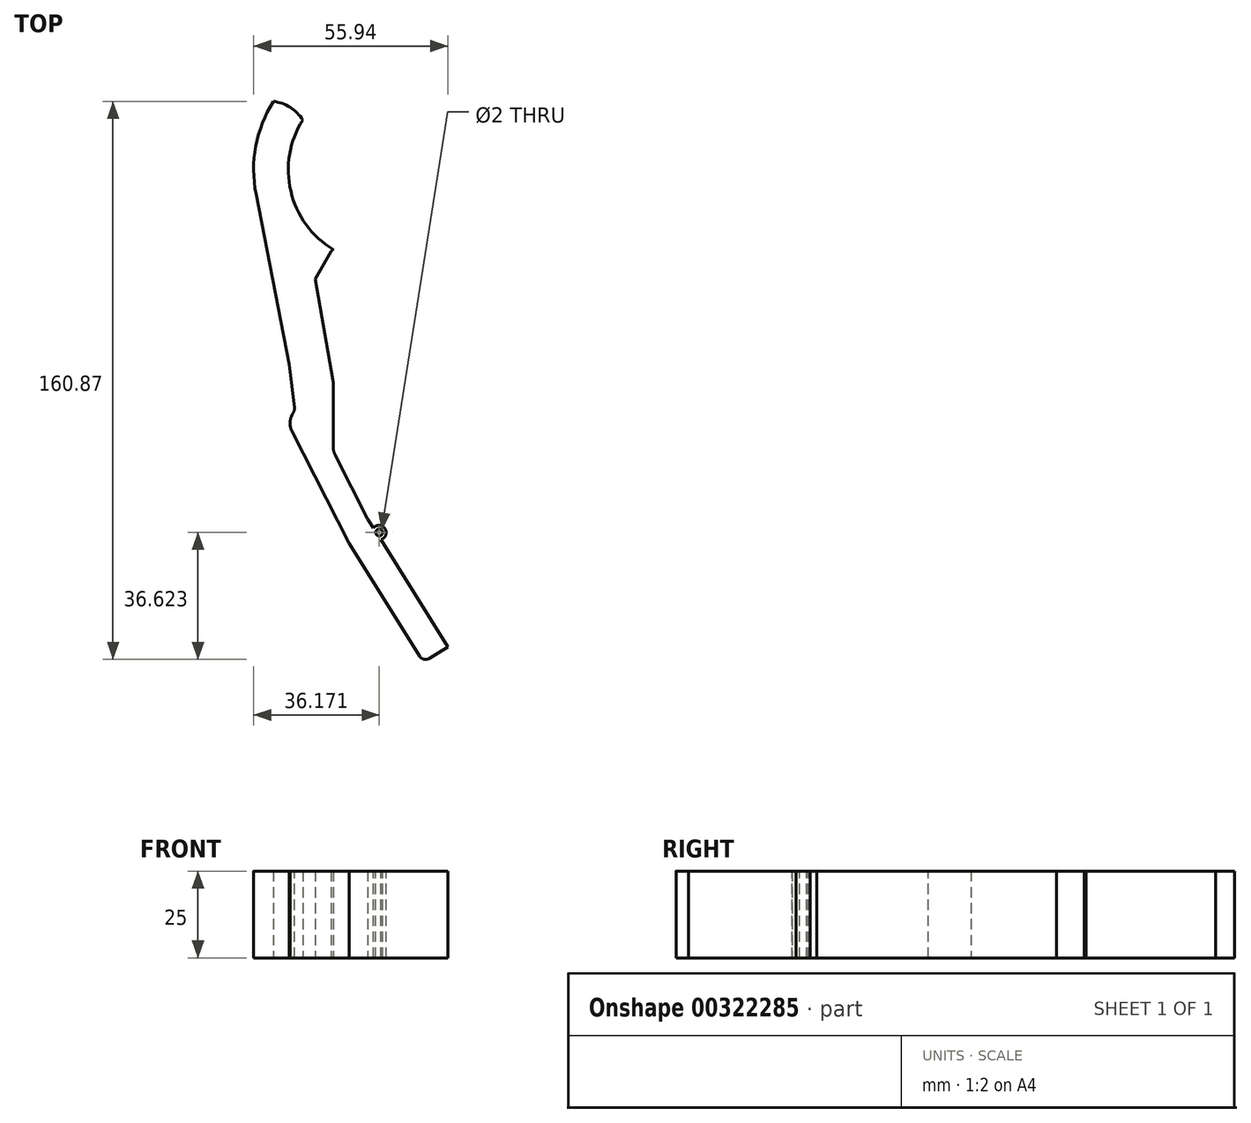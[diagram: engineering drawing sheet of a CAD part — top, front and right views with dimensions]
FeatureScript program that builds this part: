
annotation { "Feature Type Name" : "Feature", "Feature Type Description" : "" }
export const myFeature = defineFeature(function(context is Context, id is Id, definition is map)
    precondition{}
    {
        {
            var Q0;
            Q0=qCreatedBy(makeId("Top.planeOp"),FACE);
            var sketch = newSketch(context, id + "F0", { "sketchPlane" : qUnion([Q0])});
            skLineSegment(sketch, "E0", {"start": v(0, 0) * mm, "end": v(0, 10) * mm});
            skLineSegment(sketch, "E1", {"start": v(0, 10) * mm, "end": v(-23.85, 48.16) * mm});
            skLineSegment(sketch, "E2", {"start": v(-23.85, 48.16) * mm, "end": v(-46.55, 92.71) * mm});
            skLineSegment(sketch, "E3", {"start": v(-46.55, 92.71) * mm, "end": v(-56.09, 141.8) * mm});
            skLineSegment(sketch, "E4", {"start": v(0, 10) * mm, "end": v(0, 20.39) * mm});
            skLineSegment(sketch, "E5", {"start": v(0, 0) * mm, "end": v(-26.5, 42.4) * mm});
            skLineSegment(sketch, "E6", {"start": v(-26.5, 42.4) * mm, "end": v(-44.66, 78.04) * mm});
            skLineSegment(sketch, "E7", {"start": v(-44.66, 78.04) * mm, "end": v(-46.55, 92.71) * mm});
            skPoint(sketch, "E8", {"position": v(-33.83, 67.76) * mm});
            skLineSegment(sketch, "E9", {"start": v(-33.83, 67.76) * mm, "end": v(-33.83, 87.76) * mm});
            skLineSegment(sketch, "E10", {"start": v(-33.83, 87.76) * mm, "end": v(-39.04, 117.3) * mm});
            skLineSegment(sketch, "E11", {"start": v(-39.04, 117.3) * mm, "end": v(-34.04, 125.97) * mm});
            skArc(sketch, "E12", {"start": v(-56.09, 141.8) * mm, "mid": v(-50.15, 127.75) * mm, "end": v(-39.04, 117.3) * mm});
            skArc(sketch, "E13.0", {"start": v(-46.27, 143.7) * mm, "mid": v(-41.94, 133.47) * mm, "end": v(-33.85, 125.85) * mm});
            skArc(sketch, "E14", {"start": v(-33.85, 125.85) * mm, "mid": v(-46.05, 142.7) * mm, "end": v(-42.6, 163.2) * mm});
            skArc(sketch, "E15.0", {"start": v(-39.04, 117.3) * mm, "mid": v(-55.8, 140.41) * mm, "end": v(-51.06, 168.55) * mm});
            skArc(sketch, "E16", {"start": v(-42.6, 163.2) * mm, "mid": v(-46.23, 166.83) * mm, "end": v(-51.06, 168.55) * mm});
            skArc(sketch, "E17", {"start": v(-42.6, 163.2) * mm, "mid": v(-46.1, 142.68) * mm, "end": v(-33.85, 125.85) * mm});
            skArc(sketch, "E18", {"start": v(-33.85, 125.85) * mm, "mid": v(-37.1, 121.98) * mm, "end": v(-39.04, 117.3) * mm});
            skPoint(sketch, "E19", {"position": v(-21.2, 43.92) * mm});
            skSolve(sketch);
        }
        {
            var Q0;
            {var subQ1=sQuery(id+"F0.wireOp",EDGE,"E3");Q0=makeQuery(id+"F0.imprint","IMPRINT",FACE,{"disambiguationData":[TD([[makeQuery(id+"F0.imprint","IMPRINT",EDGE,{"derivedFrom":subQ1}),-1.0]])]});}
            var Q1;
            Q1=makeQuery(id+"F0.imprint","IMPRINT",FACE,{"disambiguationData":[TD([[makeQuery(id+"F0.imprint","IMPRINT",EDGE,{"derivedFrom":sQuery(id+"F0.wireOp",EDGE,"E0")}),1.0]])]});
            extrude(context, id + "F1", {"entities" : qUnion([Q0, Q1]), "depth" : 25 * mm});
        }
        {
            var Q0;
            Q0=qSketchRegion(id+"F0",true);
            extrude(context, id + "F2", {"entities" : qUnion([Q0]), "operationType" : NewBodyOperationType.ADD, "depth" : 25 * mm});
        }
        {
            var Q0;
            Q0=qCreatedBy(makeId("Top.planeOp"),FACE);
            var sketch = newSketch(context, id + "F3", { "sketchPlane" : qUnion([Q0])});
            skCircle(sketch, "E20", {"center": v(0, 0) * mm, "radius": 10.04 * mm});
            skSolve(sketch);
        }
        {
            var Q0;
            Q0=makeQuery(id+"F3.imprint","IMPRINT",FACE,{"disambiguationData":[TD([[makeQuery(id+"F3.imprint","IMPRINT",EDGE,{"derivedFrom":sQuery(id+"F3.wireOp",EDGE,"E20")}),1.0]])]});
            extrude(context, id + "F4", {"entities" : qUnion([Q0]), "operationType" : NewBodyOperationType.ADD, "depth" : 25 * mm});
        }
        {
            var Q0;
            Q0=makeQuery(id+"F1.opExtrude","SWEPT_FACE",FACE,{"disambiguationData":[OSD([sQuery(id+"F0.wireOp",EDGE,"E5")])]});
            var sketch = newSketch(context, id + "F5", { "sketchPlane" : qUnion([Q0])});
            skPoint(sketch, "E21", {"position": v(-10.04, 16.7) * mm});
            skPoint(sketch, "E22", {"position": v(-10.04, 8.4) * mm});
            skLineSegment(sketch, "E23.bottom", {"start": v(-10.04, 25) * mm, "end": v(-15.56, 25) * mm});
            skLineSegment(sketch, "E23.top", {"start": v(-10.04, 16.7) * mm, "end": v(-15.56, 16.7) * mm});
            skLineSegment(sketch, "E23.left", {"start": v(-10.04, 25) * mm, "end": v(-10.04, 16.7) * mm});
            skLineSegment(sketch, "E23.right", {"start": v(-15.56, 25) * mm, "end": v(-15.56, 16.7) * mm});
            skLineSegment(sketch, "E24.bottom", {"start": v(-10.04, 0) * mm, "end": v(-15.06, 0) * mm});
            skLineSegment(sketch, "E24.top", {"start": v(-10.04, 8.4) * mm, "end": v(-15.06, 8.4) * mm});
            skLineSegment(sketch, "E24.left", {"start": v(-10.04, 0) * mm, "end": v(-10.04, 8.4) * mm});
            skLineSegment(sketch, "E24.right", {"start": v(-15.06, 0) * mm, "end": v(-15.06, 8.4) * mm});
            skSolve(sketch);
        }
        {
            var Q0;
            Q0=makeQuery(id+"F5.imprint","IMPRINT",FACE,{"disambiguationData":[TD([[makeQuery(id+"F5.imprint","IMPRINT",EDGE,{"derivedFrom":sQuery(id+"F5.wireOp",EDGE,"E24.bottom")}),-1.0]])]});
            var Q1;
            Q1=makeQuery(id+"F5.imprint","IMPRINT",FACE,{"disambiguationData":[TD([[makeQuery(id+"F5.imprint","IMPRINT",EDGE,{"derivedFrom":sQuery(id+"F5.wireOp",EDGE,"E23.bottom")}),1.0]])]});
            extrude(context, id + "F6", {"entities" : qUnion([Q0, Q1]), "operationType" : NewBodyOperationType.ADD, "depth" : 28.7 * mm});
        }
        {
            var Q0;
            Q0=makeQuery(id+"F6.opExtrude","SWEPT_FACE",FACE,{"disambiguationData":[OSD([sQuery(id+"F5.wireOp",EDGE,"E23.left")])]});
            var Q1;
            Q1=makeQuery(id+"F6.opExtrude","SWEPT_FACE",FACE,{"disambiguationData":[OSD([sQuery(id+"F5.wireOp",EDGE,"E24.left")])]});
            extrude(context, id + "F7", {"entities" : qUnion([Q0, Q1]), "operationType" : NewBodyOperationType.REMOVE, "endBound" : BoundingType.SYMMETRIC, "oppositeDirection" : true, "depth" : 62.6 * mm});
        }
        {
            var Q0;
            {var subQ0=sQuery(id+"F3.wireOp",EDGE,"E20");var subQ1=sQuery(id+"F0.wireOp",EDGE,"E5");Q0=makeQuery(id+"F7.boolean.opBoolean","MERGE",FACE,{"derivedFrom":[makeQuery(id+"F1.opExtrude","SWEPT_FACE",FACE,{"disambiguationData":[OSD([subQ1])]}),makeQuery(id+"F7.opExtrude","SWEPT_FACE",FACE,{"disambiguationData":[OSD([subQ1,subQ0,sQuery(id+"F5.wireOp",EDGE,"E23.left")])]}),makeQuery(id+"F7.opExtrude","SWEPT_FACE",FACE,{"disambiguationData":[OSD([subQ1,subQ0,sQuery(id+"F5.wireOp",EDGE,"E24.left")])]})]});}
            var sketch = newSketch(context, id + "F8", { "sketchPlane" : qUnion([Q0])});
            skLineSegment(sketch, "E25.bottom", {"start": v(-10.04, 8.4) * mm, "end": v(10.04, 8.4) * mm});
            skLineSegment(sketch, "E25.top", {"start": v(-10.04, 0) * mm, "end": v(10.04, 0) * mm});
            skLineSegment(sketch, "E25.left", {"start": v(-10.04, 8.4) * mm, "end": v(-10.04, 0) * mm});
            skLineSegment(sketch, "E25.right", {"start": v(10.04, 8.4) * mm, "end": v(10.04, 0) * mm});
            skLineSegment(sketch, "E26.bottom", {"start": v(-10.04, 16.7) * mm, "end": v(10.04, 16.7) * mm});
            skLineSegment(sketch, "E26.top", {"start": v(-10.04, 25) * mm, "end": v(10.04, 25) * mm});
            skLineSegment(sketch, "E26.left", {"start": v(-10.04, 16.7) * mm, "end": v(-10.04, 25) * mm});
            skLineSegment(sketch, "E26.right", {"start": v(10.04, 16.7) * mm, "end": v(10.04, 25) * mm});
            skSolve(sketch);
        }
        {
            var Q0;
            Q0=makeQuery(id+"F8.imprint","IMPRINT",FACE,{"disambiguationData":[TD([[makeQuery(id+"F8.imprint","IMPRINT",EDGE,{"derivedFrom":sQuery(id+"F8.wireOp",EDGE,"E26.bottom")}),1.0]])]});
            var Q1;
            Q1=makeQuery(id+"F8.imprint","IMPRINT",FACE,{"disambiguationData":[TD([[makeQuery(id+"F8.imprint","IMPRINT",EDGE,{"derivedFrom":sQuery(id+"F8.wireOp",EDGE,"E25.bottom")}),-1.0]])]});
            extrude(context, id + "F9", {"entities" : qUnion([Q0, Q1]), "operationType" : NewBodyOperationType.REMOVE, "oppositeDirection" : true, "depth" : 25 * mm});
        }
        {
            var Q0;
            Q0=sQuery(id+"F0.wireOp",VERTEX,"E0.start");
            var Q1;
            Q1=makeQuery(id+"F1.opExtrude","SWEPT_BODY",BODY,{"disambiguationData":[OSD([sQuery(id+"F0.wireOp",EDGE,"E0"),sQuery(id+"F0.wireOp",EDGE,"E1"),sQuery(id+"F0.wireOp",EDGE,"E2"),sQuery(id+"F0.wireOp",EDGE,"E3"),sQuery(id+"F0.wireOp",EDGE,"E5"),sQuery(id+"F0.wireOp",EDGE,"E6"),sQuery(id+"F0.wireOp",EDGE,"E7"),sQuery(id+"F0.wireOp",EDGE,"E9"),sQuery(id+"F0.wireOp",EDGE,"E10"),sQuery(id+"F0.wireOp",EDGE,"E15.0")])]});
            hole(context, id + "F10", {"style" : HoleStyle.SIMPLE, "endStyle" : HoleEndStyle.THROUGH, "oppositeDirection" : true, "holeDiameter" : 15 * mm, "tappedDepth" : 12 * mm, "tapClearance" : 3, "locations" : qUnion([Q0]), "scope" : qUnion([Q1])});
        }
        {
            var Q0;
            {var subQ0=sQuery(id+"F3.wireOp",EDGE,"E20");var subQ1=sQuery(id+"F0.wireOp",EDGE,"E5");Q0=makeQuery(id+"F7.boolean.opBoolean","MERGE",FACE,{"derivedFrom":[makeQuery(id+"F1.opExtrude","SWEPT_FACE",FACE,{"disambiguationData":[OSD([subQ1])]}),makeQuery(id+"F7.opExtrude","SWEPT_FACE",FACE,{"disambiguationData":[OSD([subQ1,subQ0,sQuery(id+"F5.wireOp",EDGE,"E23.left")])]}),makeQuery(id+"F7.opExtrude","SWEPT_FACE",FACE,{"disambiguationData":[OSD([subQ1,subQ0,sQuery(id+"F5.wireOp",EDGE,"E24.left")])]})]});}
            extrude(context, id + "F11", {"entities" : qUnion([Q0]), "operationType" : NewBodyOperationType.ADD, "depth" : 3 * mm});
        }
        {
            var Q0;
            Q0=makeQuery(id+"F1.opExtrude","SWEPT_FACE",FACE,{"disambiguationData":[OSD([sQuery(id+"F0.wireOp",EDGE,"E6")])]});
            extrude(context, id + "F12", {"entities" : qUnion([Q0]), "operationType" : NewBodyOperationType.ADD, "depth" : 3 * mm});
        }
        {
            var Q0;
            Q0=makeQuery(id+"F11.opExtrude","SWEPT_FACE",FACE,{"disambiguationData":[OSD([sQuery(id+"F0.wireOp",EDGE,"E5"),sQuery(id+"F0.wireOp",EDGE,"E6")])]});
            extrude(context, id + "F13", {"entities" : qUnion([Q0]), "operationType" : NewBodyOperationType.ADD, "depth" : 0.4 * mm});
        }
        {
            var Q0;
            {var subQ0=sQuery(id+"F0.wireOp",EDGE,"E6");var subQ1=sQuery(id+"F0.wireOp",EDGE,"E5");var subQ2=sQuery(id+"F5.wireOp",EDGE,"E23.bottom");var subQ3=sQuery(id+"F3.wireOp",EDGE,"E20");var subQ4=sQuery(id+"F0.wireOp",EDGE,"E15.0");var subQ5=sQuery(id+"F0.wireOp",EDGE,"E10");var subQ6=sQuery(id+"F0.wireOp",EDGE,"E9");var subQ7=sQuery(id+"F0.wireOp",EDGE,"E7");var subQ8=sQuery(id+"F0.wireOp",EDGE,"E3");var subQ9=sQuery(id+"F0.wireOp",EDGE,"E2");var subQ10=sQuery(id+"F0.wireOp",EDGE,"E1");var subQ11=sQuery(id+"F0.wireOp",EDGE,"E0");Q0=makeQuery(id+"F13.boolean.opBoolean","MERGE",FACE,{"derivedFrom":[makeQuery(id+"F12.boolean.opBoolean","MERGE",FACE,{"derivedFrom":[makeQuery(id+"F11.boolean.opBoolean","MERGE",FACE,{"derivedFrom":[makeQuery(id+"F6.boolean.opBoolean","MERGE",FACE,{"derivedFrom":[makeQuery(id+"F4.boolean.opBoolean","MERGE",FACE,{"derivedFrom":[makeQuery(id+"F2.boolean.opBoolean","MERGE",FACE,{"derivedFrom":[makeQuery(id+"F1.opExtrude","CAP_FACE",FACE,{"disambiguationData":[OSD([subQ11,subQ10,subQ9,subQ8,subQ1,subQ0,subQ7,subQ6,subQ5,subQ4])],"isStart":false}),makeQuery(id+"F2.opExtrude","CAP_FACE",FACE,{"disambiguationData":[OSD([subQ11,subQ10,subQ9,subQ8,subQ1,subQ0,subQ7,subQ6,subQ5,sQuery(id+"F0.wireOp",EDGE,"E11"),sQuery(id+"F0.wireOp",EDGE,"E14"),subQ4,sQuery(id+"F0.wireOp",EDGE,"E16"),sQuery(id+"F0.wireOp",EDGE,"E18")])],"isStart":false})]}),makeQuery(id+"F4.opExtrude","CAP_FACE",FACE,{"disambiguationData":[OSD([subQ3])],"isStart":false})]}),makeQuery(id+"F6.opExtrude","SWEPT_FACE",FACE,{"disambiguationData":[OSD([subQ2])]})]}),makeQuery(id+"F11.opExtrude","SWEPT_FACE",FACE,{"disambiguationData":[OSD([subQ1,subQ3,subQ2,sQuery(id+"F5.wireOp",EDGE,"E23.left")])]})]}),makeQuery(id+"F12.opExtrude","SWEPT_FACE",FACE,{"disambiguationData":[OSD([subQ0]),TDD([makeQuery(id+"F1.opExtrude","CAP_EDGE",EDGE,{"disambiguationData":[OSD([subQ0])],"isStart":false})])]})]}),makeQuery(id+"F13.opExtrude","SWEPT_FACE",FACE,{"disambiguationData":[OSD([subQ1,subQ0]),TDD([makeQuery(id+"F11.opExtrude","SWEPT_EDGE",EDGE,{"disambiguationData":[OSD([subQ1,subQ0]),TDD([makeQuery(id+"F1.opExtrude","CAP_VERTEX",VERTEX,{"disambiguationData":[OSD([subQ1,subQ0])],"isStart":false})])]})])]})]});}
            var sketch = newSketch(context, id + "F14", { "sketchPlane" : qUnion([Q0])});
            skArc(sketch, "E27", {"start": v(-47.33, 76.68) * mm, "mid": v(-45.27, 78.9) * mm, "end": v(-45.16, 81.94) * mm});
            skSolve(sketch);
        }
        {
            var Q0;
            Q0=qSketchRegion(id+"F14",true);
            var Q1;
            {var subQ1=sQuery(id+"F0.wireOp",EDGE,"E6");var subQ2=sQuery(id+"F0.wireOp",EDGE,"E7");var subQ3=makeQuery(id+"F12.opExtrude","SWEPT_EDGE",EDGE,{"disambiguationData":[OSD([subQ1,subQ2]),TDD([makeQuery(id+"F1.opExtrude","CAP_VERTEX",VERTEX,{"disambiguationData":[OSD([subQ1,subQ2])],"isStart":false})])]});Q1=makeQuery(id+"F14.imprint","IMPRINT",FACE,{"disambiguationData":[TD([[makeQuery(id+"F14.imprint","IMPRINT",EDGE,{"derivedFrom":subQ3}),1.0]])]});}
            extrude(context, id + "F15", {"entities" : qUnion([Q0, Q1]), "operationType" : NewBodyOperationType.ADD, "oppositeDirection" : true, "depth" : 25 * mm});
        }
        {
            var Q0;
            {var subQ0=sQuery(id+"F0.wireOp",EDGE,"E7");var subQ1=sQuery(id+"F0.wireOp",EDGE,"E6");Q0=makeQuery(id+"F15.boolean.opBoolean","MERGE",EDGE,{"derivedFrom":[makeQuery(id+"F12.opExtrude","CAP_EDGE",EDGE,{"disambiguationData":[OSD([subQ1,subQ0])],"isStart":false}),makeQuery(id+"F15.opExtrude","SWEPT_EDGE",EDGE,{"disambiguationData":[OSD([subQ1,subQ0,sQuery(id+"F14.wireOp",EDGE,"E27")])]})]});}
            fillet(context, id + "F16", {"entities" : qUnion([Q0]), "radius" : 5 * mm, "tangentPropagation" : true, "allowEdgeOverflow" : false});
        }
        {
            var Q0;
            Q0=makeQuery(id+"F1.opExtrude","SWEPT_EDGE",EDGE,{"disambiguationData":[OSD([sQuery(id+"F0.wireOp",EDGE,"E2"),sQuery(id+"F0.wireOp",EDGE,"E9")])]});
            fillet(context, id + "F17", {"entities" : qUnion([Q0]), "radius" : 5 * mm, "tangentPropagation" : true, "allowEdgeOverflow" : false});
        }
        {
            var Q0;
            Q0=makeQuery(id+"F1.opExtrude","SWEPT_EDGE",EDGE,{"disambiguationData":[OSD([sQuery(id+"F0.wireOp",EDGE,"E9"),sQuery(id+"F0.wireOp",EDGE,"E10")])]});
            fillet(context, id + "F18", {"entities" : qUnion([Q0]), "radius" : 5 * mm, "tangentPropagation" : true, "allowEdgeOverflow" : false});
        }
        {
            var Q0;
            {var subQ0=sQuery(id+"F0.wireOp",EDGE,"E7");var subQ1=sQuery(id+"F0.wireOp",EDGE,"E6");var subQ2=sQuery(id+"F0.wireOp",EDGE,"E5");var subQ3=sQuery(id+"F5.wireOp",EDGE,"E23.bottom");var subQ4=sQuery(id+"F3.wireOp",EDGE,"E20");var subQ5=sQuery(id+"F0.wireOp",EDGE,"E15.0");var subQ6=sQuery(id+"F0.wireOp",EDGE,"E10");var subQ7=sQuery(id+"F0.wireOp",EDGE,"E9");var subQ8=sQuery(id+"F0.wireOp",EDGE,"E3");var subQ9=sQuery(id+"F0.wireOp",EDGE,"E2");var subQ10=sQuery(id+"F0.wireOp",EDGE,"E1");var subQ11=sQuery(id+"F0.wireOp",EDGE,"E0");Q0=makeQuery(id+"F15.boolean.opBoolean","MERGE",FACE,{"derivedFrom":[makeQuery(id+"F13.boolean.opBoolean","MERGE",FACE,{"derivedFrom":[makeQuery(id+"F12.boolean.opBoolean","MERGE",FACE,{"derivedFrom":[makeQuery(id+"F11.boolean.opBoolean","MERGE",FACE,{"derivedFrom":[makeQuery(id+"F6.boolean.opBoolean","MERGE",FACE,{"derivedFrom":[makeQuery(id+"F4.boolean.opBoolean","MERGE",FACE,{"derivedFrom":[makeQuery(id+"F2.boolean.opBoolean","MERGE",FACE,{"derivedFrom":[makeQuery(id+"F1.opExtrude","CAP_FACE",FACE,{"disambiguationData":[OSD([subQ11,subQ10,subQ9,subQ8,subQ2,subQ1,subQ0,subQ7,subQ6,subQ5])],"isStart":false}),makeQuery(id+"F2.opExtrude","CAP_FACE",FACE,{"disambiguationData":[OSD([subQ11,subQ10,subQ9,subQ8,subQ2,subQ1,subQ0,subQ7,subQ6,sQuery(id+"F0.wireOp",EDGE,"E11"),sQuery(id+"F0.wireOp",EDGE,"E14"),subQ5,sQuery(id+"F0.wireOp",EDGE,"E16"),sQuery(id+"F0.wireOp",EDGE,"E18")])],"isStart":false})]}),makeQuery(id+"F4.opExtrude","CAP_FACE",FACE,{"disambiguationData":[OSD([subQ4])],"isStart":false})]}),makeQuery(id+"F6.opExtrude","SWEPT_FACE",FACE,{"disambiguationData":[OSD([subQ3])]})]}),makeQuery(id+"F11.opExtrude","SWEPT_FACE",FACE,{"disambiguationData":[OSD([subQ2,subQ4,subQ3,sQuery(id+"F5.wireOp",EDGE,"E23.left")])]})]}),makeQuery(id+"F12.opExtrude","SWEPT_FACE",FACE,{"disambiguationData":[OSD([subQ1]),TDD([makeQuery(id+"F1.opExtrude","CAP_EDGE",EDGE,{"disambiguationData":[OSD([subQ1])],"isStart":false})])]})]}),makeQuery(id+"F13.opExtrude","SWEPT_FACE",FACE,{"disambiguationData":[OSD([subQ2,subQ1]),TDD([makeQuery(id+"F11.opExtrude","SWEPT_EDGE",EDGE,{"disambiguationData":[OSD([subQ2,subQ1]),TDD([makeQuery(id+"F1.opExtrude","CAP_VERTEX",VERTEX,{"disambiguationData":[OSD([subQ2,subQ1])],"isStart":false})])]})])]})]}),makeQuery(id+"F15.opExtrude","CAP_FACE",FACE,{"disambiguationData":[OSD([subQ1,subQ0,sQuery(id+"F14.wireOp",EDGE,"E27")])],"isStart":true})]});}
            var sketch = newSketch(context, id + "F19", { "sketchPlane" : qUnion([Q0])});
            skPoint(sketch, "E28", {"position": v(-21.2, 43.92) * mm});
            skPoint(sketch, "E29", {"position": v(-22.26, 45.62) * mm});
            skPoint(sketch, "E30", {"position": v(-20.14, 42.23) * mm});
            skArc(sketch, "E31", {"start": v(-20.14, 42.23) * mm, "mid": v(-18.9, 45.36) * mm, "end": v(-22.26, 45.62) * mm});
            skSolve(sketch);
        }
        {
            var Q0;
            Q0=qSketchRegion(id+"F19",true);
            var Q1;
            {var subQ0=sQuery(id+"F19.wireOp",EDGE,"E31");Q1=makeQuery(id+"F19.imprint","IMPRINT",FACE,{"disambiguationData":[TD([[makeQuery(id+"F19.imprint","IMPRINT",EDGE,{"derivedFrom":subQ0}),1.0]])]});}
            extrude(context, id + "F20", {"entities" : qUnion([Q0, Q1]), "operationType" : NewBodyOperationType.ADD, "oppositeDirection" : true, "depth" : 25 * mm});
        }
        {
            var Q0;
            {var subQ0=sQuery(id+"F0.wireOp",EDGE,"E1");var subQ1=sQuery(id+"F0.wireOp",EDGE,"E7");var subQ2=sQuery(id+"F0.wireOp",EDGE,"E6");var subQ3=sQuery(id+"F0.wireOp",EDGE,"E5");var subQ4=sQuery(id+"F5.wireOp",EDGE,"E23.bottom");var subQ5=sQuery(id+"F3.wireOp",EDGE,"E20");var subQ6=sQuery(id+"F0.wireOp",EDGE,"E15.0");var subQ7=sQuery(id+"F0.wireOp",EDGE,"E10");var subQ8=sQuery(id+"F0.wireOp",EDGE,"E9");var subQ9=sQuery(id+"F0.wireOp",EDGE,"E3");var subQ10=sQuery(id+"F0.wireOp",EDGE,"E2");var subQ11=sQuery(id+"F0.wireOp",EDGE,"E0");Q0=makeQuery(id+"F20.boolean.opBoolean","MERGE",FACE,{"derivedFrom":[makeQuery(id+"F15.boolean.opBoolean","MERGE",FACE,{"derivedFrom":[makeQuery(id+"F13.boolean.opBoolean","MERGE",FACE,{"derivedFrom":[makeQuery(id+"F12.boolean.opBoolean","MERGE",FACE,{"derivedFrom":[makeQuery(id+"F11.boolean.opBoolean","MERGE",FACE,{"derivedFrom":[makeQuery(id+"F6.boolean.opBoolean","MERGE",FACE,{"derivedFrom":[makeQuery(id+"F4.boolean.opBoolean","MERGE",FACE,{"derivedFrom":[makeQuery(id+"F2.boolean.opBoolean","MERGE",FACE,{"derivedFrom":[makeQuery(id+"F1.opExtrude","CAP_FACE",FACE,{"disambiguationData":[OSD([subQ11,subQ0,subQ10,subQ9,subQ3,subQ2,subQ1,subQ8,subQ7,subQ6])],"isStart":false}),makeQuery(id+"F2.opExtrude","CAP_FACE",FACE,{"disambiguationData":[OSD([subQ11,subQ0,subQ10,subQ9,subQ3,subQ2,subQ1,subQ8,subQ7,sQuery(id+"F0.wireOp",EDGE,"E11"),sQuery(id+"F0.wireOp",EDGE,"E14"),subQ6,sQuery(id+"F0.wireOp",EDGE,"E16"),sQuery(id+"F0.wireOp",EDGE,"E18")])],"isStart":false})]}),makeQuery(id+"F4.opExtrude","CAP_FACE",FACE,{"disambiguationData":[OSD([subQ5])],"isStart":false})]}),makeQuery(id+"F6.opExtrude","SWEPT_FACE",FACE,{"disambiguationData":[OSD([subQ4])]})]}),makeQuery(id+"F11.opExtrude","SWEPT_FACE",FACE,{"disambiguationData":[OSD([subQ3,subQ5,subQ4,sQuery(id+"F5.wireOp",EDGE,"E23.left")])]})]}),makeQuery(id+"F12.opExtrude","SWEPT_FACE",FACE,{"disambiguationData":[OSD([subQ2]),TDD([makeQuery(id+"F1.opExtrude","CAP_EDGE",EDGE,{"disambiguationData":[OSD([subQ2])],"isStart":false})])]})]}),makeQuery(id+"F13.opExtrude","SWEPT_FACE",FACE,{"disambiguationData":[OSD([subQ3,subQ2]),TDD([makeQuery(id+"F11.opExtrude","SWEPT_EDGE",EDGE,{"disambiguationData":[OSD([subQ3,subQ2]),TDD([makeQuery(id+"F1.opExtrude","CAP_VERTEX",VERTEX,{"disambiguationData":[OSD([subQ3,subQ2])],"isStart":false})])]})])]})]}),makeQuery(id+"F15.opExtrude","CAP_FACE",FACE,{"disambiguationData":[OSD([subQ2,subQ1,sQuery(id+"F14.wireOp",EDGE,"E27")])],"isStart":true})]}),makeQuery(id+"F20.opExtrude","CAP_FACE",FACE,{"disambiguationData":[OSD([subQ0,sQuery(id+"F19.wireOp",EDGE,"E31")])],"isStart":true})]});}
            var sketch = newSketch(context, id + "F21", { "sketchPlane" : qUnion([Q0])});
            skPoint(sketch, "E32", {"position": v(-20.59, 44.3) * mm});
            skCircle(sketch, "E33", {"center": v(-20.59, 44.3) * mm, "radius": 1 * mm});
            skSolve(sketch);
        }
        {
            var Q0;
            Q0=qSketchRegion(id+"F21",true);
            extrude(context, id + "F22", {"entities" : qUnion([Q0]), "operationType" : NewBodyOperationType.REMOVE, "oppositeDirection" : true, "depth" : 25 * mm});
        }
        {
            var Q0;
            Q0=makeQuery(id+"F9.boolean.opBoolean","MERGE",FACE,{"derivedFrom":[makeQuery(id+"F7.boolean.opBoolean","COPY",FACE,{"derivedFrom":makeQuery(id+"F7.opExtrude","SWEPT_FACE",FACE,{"disambiguationData":[OSD([sQuery(id+"F0.wireOp",EDGE,"E5"),sQuery(id+"F3.wireOp",EDGE,"E20"),sQuery(id+"F5.wireOp",EDGE,"E23.top"),sQuery(id+"F5.wireOp",EDGE,"E23.left")])]})}),makeQuery(id+"F9.opExtrude","SWEPT_FACE",FACE,{"disambiguationData":[OSD([sQuery(id+"F8.wireOp",EDGE,"E26.bottom")])]})]});
            var sketch = newSketch(context, id + "F23", { "sketchPlane" : qUnion([Q0])});
            skLineSegment(sketch, "E34", {"start": v(-21.58, -2.98) * mm, "end": v(2.67, -15.5) * mm});
            skLineSegment(sketch, "E35", {"start": v(2.67, -15.5) * mm, "end": v(23.1, 1.13) * mm});
            skLineSegment(sketch, "E36", {"start": v(23.1, 1.13) * mm, "end": v(-0.82, 11.32) * mm});
            skLineSegment(sketch, "E37", {"start": v(-0.82, 11.32) * mm, "end": v(-21.58, -1.65) * mm});
            skLineSegment(sketch, "E38", {"start": v(-21.58, -1.65) * mm, "end": v(-21.58, -2.98) * mm});
            skSolve(sketch);
        }
        {
            var Q0;
            Q0 = qSketchRegion(id + "F23", true);
            extrude(context, id + "F24", {"entities" : qUnion([Q0]), "operationType" : NewBodyOperationType.REMOVE, "oppositeDirection" : true, "depth" : 25 * mm});
        }
        {
            var Q0;
            {var subQ0=sQuery(id+"F0.wireOp",EDGE,"E1");var subQ1=makeQuery(id+"F1.opExtrude","SWEPT_FACE",FACE,{"disambiguationData":[OSD([subQ0])]});Q0=makeQuery(id+"F24.boolean.opBoolean","MERGE",EDGE,{"derivedFrom":[makeQuery(id+"F9.boolean.opBoolean","INTERSECT",EDGE,{"derivedFrom":[subQ1,makeQuery(id+"F9.opExtrude","SWEPT_FACE",FACE,{"disambiguationData":[OSD([sQuery(id+"F8.wireOp",EDGE,"E25.left")])]})]}),makeQuery(id+"F9.boolean.opBoolean","INTERSECT",EDGE,{"derivedFrom":[subQ1,makeQuery(id+"F9.opExtrude","SWEPT_FACE",FACE,{"disambiguationData":[OSD([sQuery(id+"F8.wireOp",EDGE,"E26.left")])]})]}),makeQuery(id+"F24.opExtrude","SWEPT_EDGE",EDGE,{"disambiguationData":[OSD([subQ0,sQuery(id+"F8.wireOp",EDGE,"E26.bottom"),sQuery(id+"F23.wireOp",EDGE,"E36"),sQuery(id+"F23.wireOp",EDGE,"E37")])]})]});}
            var Q1;
            Q1=makeQuery(id+"F11.opExtrude","CAP_EDGE",EDGE,{"disambiguationData":[OSD([sQuery(id+"F0.wireOp",EDGE,"E5"),sQuery(id+"F3.wireOp",EDGE,"E20"),sQuery(id+"F8.wireOp",EDGE,"E25.left"),sQuery(id+"F8.wireOp",EDGE,"E26.left")])],"isStart":false});
            fillet(context, id + "F25", {"entities" : qUnion([Q0, Q1]), "radius" : 2 * mm, "tangentPropagation" : true, "allowEdgeOverflow" : false});
        }
    });
